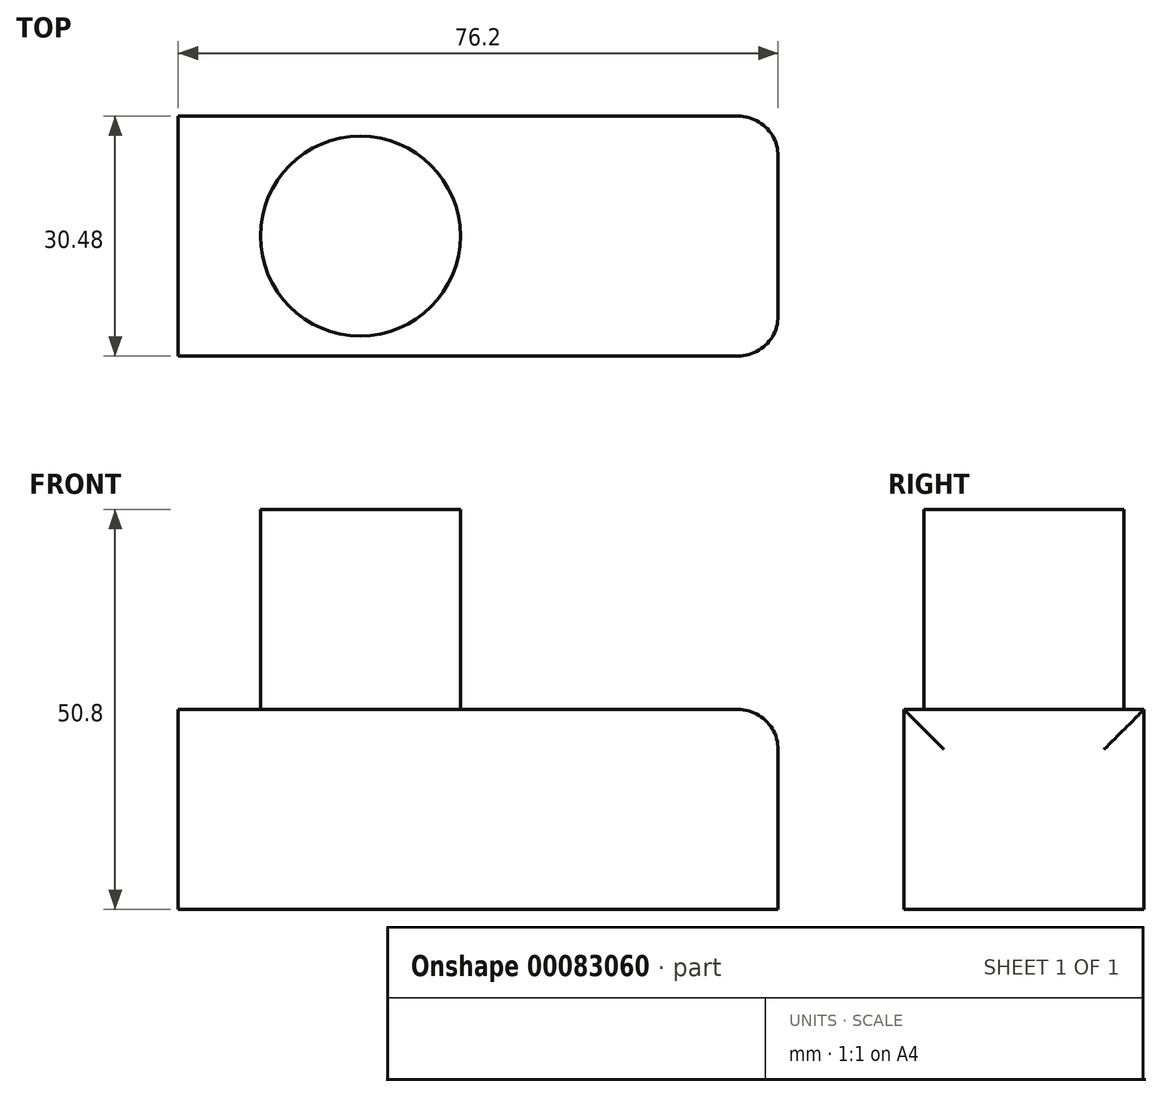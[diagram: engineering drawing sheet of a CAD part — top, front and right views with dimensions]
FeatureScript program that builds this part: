
annotation { "Feature Type Name" : "Feature", "Feature Type Description" : "" }
export const myFeature = defineFeature(function(context is Context, id is Id, definition is map)
    precondition{}
    {
        {
            var Q0;
            Q0=qCreatedBy(makeId("Top.planeOp"),FACE);
            var sketch = newSketch(context, id + "F0", { "sketchPlane" : qUnion([Q0])});
            skLineSegment(sketch, "E0.bottom", {"start": v(-38.1, 15.24) * mm, "end": v(38.1, 15.24) * mm});
            skLineSegment(sketch, "E0.top", {"start": v(-38.1, -15.24) * mm, "end": v(38.1, -15.24) * mm});
            skLineSegment(sketch, "E0.left", {"start": v(-38.1, 15.24) * mm, "end": v(-38.1, -15.24) * mm});
            skLineSegment(sketch, "E0.right", {"start": v(38.1, 15.24) * mm, "end": v(38.1, -15.24) * mm});
            skPoint(sketch, "E0.middle", {"position": v(0, 0) * mm});
            skSolve(sketch);
        }
        {
            var Q0;
            Q0 = qSketchRegion(id + "F0", true);
            extrude(context, id + "F1", {"entities" : qUnion([Q0]), "depth" : 25.4 * mm});
        }
        {
            var Q0;
            Q0=makeQuery(id+"F1.opExtrude","CAP_EDGE",EDGE,{"disambiguationData":[OSD([sQuery(id+"F0.wireOp",EDGE,"E0.right")])],"isStart":false});
            var Q1;
            Q1=makeQuery(id+"F1.opExtrude","SWEPT_EDGE",EDGE,{"disambiguationData":[OSD([sQuery(id+"F0.wireOp",EDGE,"E0.top"),sQuery(id+"F0.wireOp",EDGE,"E0.right")])]});
            var Q2;
            Q2=makeQuery(id+"F1.opExtrude","SWEPT_EDGE",EDGE,{"disambiguationData":[OSD([sQuery(id+"F0.wireOp",EDGE,"E0.bottom"),sQuery(id+"F0.wireOp",EDGE,"E0.right")])]});
            fillet(context, id + "F2", {"entities" : qUnion([Q0, Q1, Q2]), "radius" : 5.08 * mm, "tangentPropagation" : true, "allowEdgeOverflow" : false});
        }
        {
            var Q0;
            Q0=makeQuery(id+"F1.opExtrude","CAP_FACE",FACE,{"disambiguationData":[OSD([sQuery(id+"F0.wireOp",EDGE,"E0.bottom"),sQuery(id+"F0.wireOp",EDGE,"E0.top"),sQuery(id+"F0.wireOp",EDGE,"E0.left"),sQuery(id+"F0.wireOp",EDGE,"E0.right")])],"isStart":false});
            var sketch = newSketch(context, id + "F3", { "sketchPlane" : qUnion([Q0])});
            skSolve(sketch);
        }
        {
            var Q0;
            {var subQ0=sQuery(id+"F0.wireOp",EDGE,"E0.left");Q0=makeQuery(id+"F3.imprint","IMPRINT",FACE,{"disambiguationData":[TD([[makeQuery(id+"F3.imprint","IMPRINT",EDGE,{"derivedFrom":makeQuery(id+"F1.opExtrude","CAP_EDGE",EDGE,{"disambiguationData":[OSD([subQ0])],"isStart":false})}),1.0]])]});}
            var sketch = newSketch(context, id + "F4", { "sketchPlane" : qUnion([Q0])});
            skCircle(sketch, "E1", {"center": v(-14.96, 0) * mm, "radius": 12.7 * mm});
            skSolve(sketch);
        }
        {
            var Q0;
            Q0=makeQuery(id+"F4.imprint","IMPRINT",FACE,{"disambiguationData":[TD([[makeQuery(id+"F4.imprint","IMPRINT",EDGE,{"derivedFrom":sQuery(id+"F4.wireOp",EDGE,"E1")}),1.0]])]});
            extrude(context, id + "F5", {"entities" : qUnion([Q0]), "operationType" : NewBodyOperationType.ADD, "depth" : 25.4 * mm});
        }
    });
